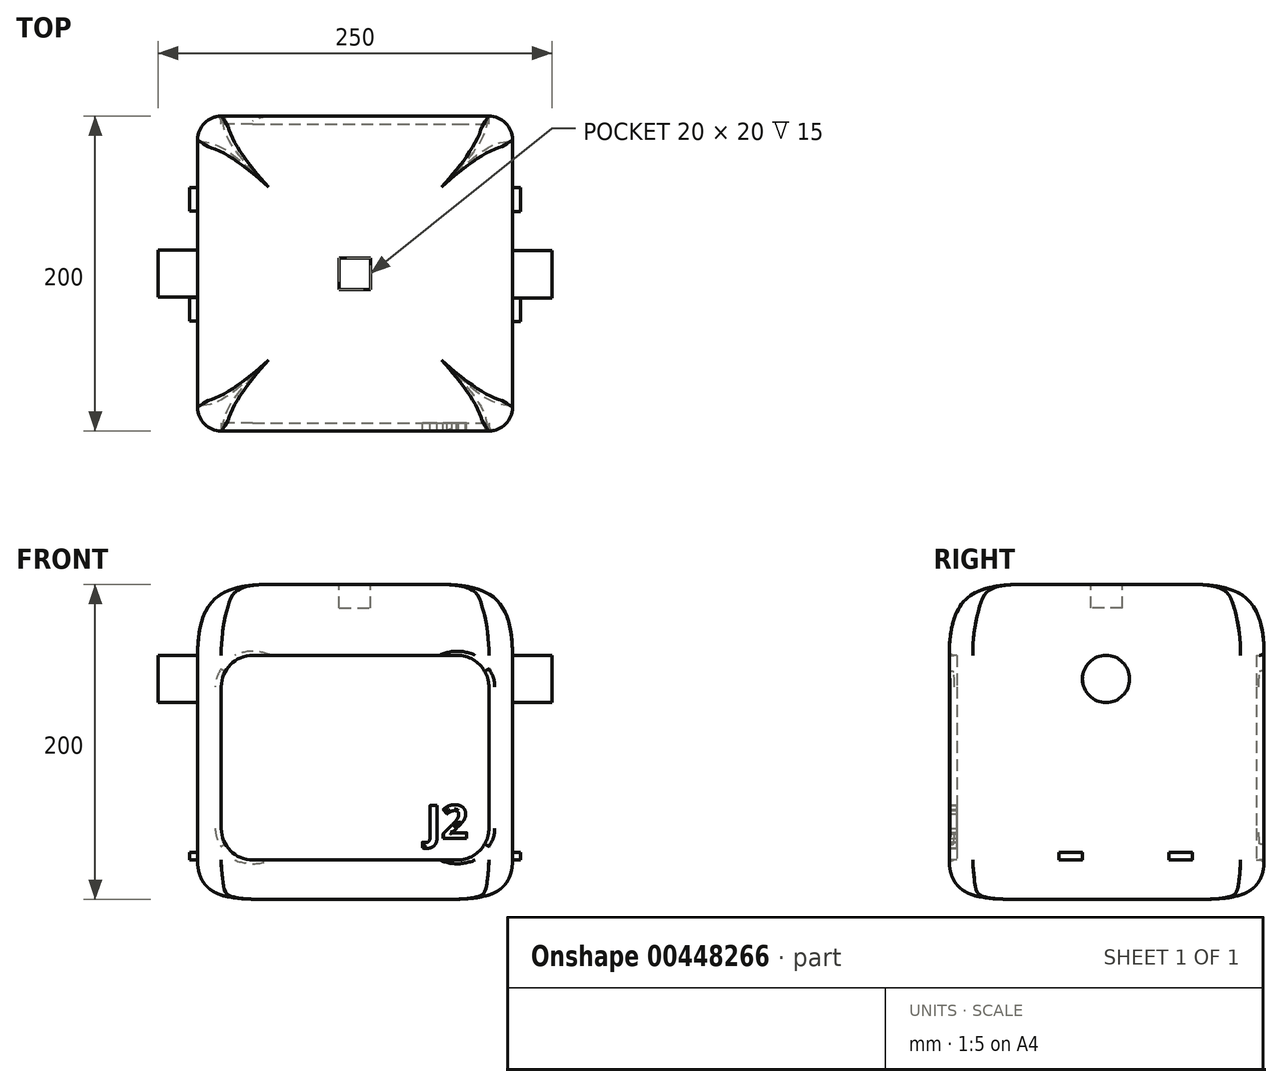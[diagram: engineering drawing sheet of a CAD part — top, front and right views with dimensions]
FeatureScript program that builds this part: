
annotation { "Feature Type Name" : "Feature", "Feature Type Description" : "" }
export const myFeature = defineFeature(function(context is Context, id is Id, definition is map)
    precondition{}
    {
        {
            var Q0;
            Q0=qCreatedBy(makeId("Front.planeOp"),FACE);
            var sketch = newSketch(context, id + "F0", { "sketchPlane" : qUnion([Q0])});
            skLineSegment(sketch, "E0.left", {"start": v(-100, 55) * mm, "end": v(-100, -75) * mm});
            skLineSegment(sketch, "E0.right", {"start": v(100, 100) * mm, "end": v(100, 90) * mm});
            skLineSegment(sketch, "E1.bottom", {"start": v(100, 100) * mm, "end": v(-100, 100) * mm, "construction": true});
            skLineSegment(sketch, "E1.top", {"start": v(100, -100) * mm, "end": v(-100, -100) * mm, "construction": true});
            skLineSegment(sketch, "E1.left", {"start": v(100, 100) * mm, "end": v(100, -100) * mm, "construction": true});
            skLineSegment(sketch, "E1.right", {"start": v(-100, 100) * mm, "end": v(-100, -100) * mm, "construction": true});
            skLineSegment(sketch, "E2", {"start": v(0, 100) * mm, "end": v(0, -100) * mm, "construction": true});
            skLineSegment(sketch, "E3", {"start": v(-100, 0) * mm, "end": v(100, 0) * mm, "construction": true});
            skLineSegment(sketch, "E4", {"start": v(100, -75) * mm, "end": v(-100, -75) * mm, "construction": true});
            skLineSegment(sketch, "E5", {"start": v(-100, 55) * mm, "end": v(100, 55) * mm, "construction": true});
            skLineSegment(sketch, "E6", {"start": v(-55, 100) * mm, "end": v(-55, -100) * mm, "construction": true});
            skLineSegment(sketch, "E7", {"start": v(55, 100) * mm, "end": v(55, -100) * mm, "construction": true});
            skLineSegment(sketch, "E8", {"start": v(-70, 100) * mm, "end": v(-70, -100) * mm, "construction": true});
            skLineSegment(sketch, "E9", {"start": v(70, 100) * mm, "end": v(70, -100) * mm, "construction": true});
            skLineSegment(sketch, "E10", {"start": v(-100, 70) * mm, "end": v(100, 70) * mm, "construction": true});
            skLineSegment(sketch, "E11", {"start": v(-100, -85) * mm, "end": v(100, -85) * mm, "construction": true});
            skLineSegment(sketch, "E12", {"start": v(-90, 100) * mm, "end": v(-90, -100) * mm, "construction": true});
            skLineSegment(sketch, "E13", {"start": v(90, 100) * mm, "end": v(90, -100) * mm, "construction": true});
            skLineSegment(sketch, "E14", {"start": v(-100, 90) * mm, "end": v(100, 90) * mm, "construction": true});
            skLineSegment(sketch, "E15", {"start": v(-100, -95) * mm, "end": v(100, -95) * mm, "construction": true});
            skFitSpline(sketch, "E16", {"points": [v(-55, 100) * mm, v(-90, 90) * mm, v(-100, 55) * mm], "startDerivative": vector(-90, 0) * mm, "endDerivative": vector(0, -90) * mm});
            skFitSpline(sketch, "E17", {"points": [v(55, 100) * mm, v(90, 90) * mm, v(100, 55) * mm], "startDerivative": vector(90, 0) * mm, "endDerivative": vector(0, -90) * mm});
            skFitSpline(sketch, "E18", {"points": [v(-55, -100) * mm, v(-90, -95) * mm, v(-100, -75) * mm], "startDerivative": vector(-80.79, 0) * mm, "endDerivative": vector(0, 67.72) * mm});
            skFitSpline(sketch, "E19", {"points": [v(55, -100) * mm, v(90, -95) * mm, v(100, -75) * mm], "startDerivative": vector(80.79, 0) * mm, "endDerivative": vector(0, 67.72) * mm});
            skLineSegment(sketch, "E20.trimOffspring", {"start": v(-55, 100) * mm, "end": v(55, 100) * mm});
            skLineSegment(sketch, "E21.trimOffspring", {"start": v(100, 55) * mm, "end": v(100, -75) * mm});
            skLineSegment(sketch, "E22.trimOffspring", {"start": v(-55, -100) * mm, "end": v(55, -100) * mm});
            skLineSegment(sketch, "E23", {"start": v(-100, -100) * mm, "end": v(100, -100) * mm, "construction": true});
            skLineSegment(sketch, "E24", {"start": v(-100, 100) * mm, "end": v(100, 100) * mm, "construction": true});
            skLineSegment(sketch, "E25", {"start": v(-100, -100) * mm, "end": v(-100, 100) * mm, "construction": true});
            skLineSegment(sketch, "E26", {"start": v(100, -100) * mm, "end": v(100, 100) * mm, "construction": true});
            skSolve(sketch);
        }
        {
            var Q0;
            Q0=makeQuery(id+"F0.imprint","IMPRINT",FACE,{"disambiguationData":[TD([[makeQuery(id+"F0.imprint","IMPRINT",EDGE,{"derivedFrom":sQuery(id+"F0.wireOp",EDGE,"E0.left")}),1.0]])]});
            extrude(context, id + "F1", {"entities" : qUnion([Q0]), "depth" : 200 * mm});
        }
        {
            var Q0;
            Q0=makeQuery(id+"F1.opExtrude","SWEPT_FACE",FACE,{"disambiguationData":[OSD([sQuery(id+"F0.wireOp",EDGE,"E21.trimOffspring")])]});
            var sketch = newSketch(context, id + "F2", { "sketchPlane" : qUnion([Q0])});
            skLineSegment(sketch, "E27", {"start": v(0, 100) * mm, "end": v(0, -100) * mm, "construction": true});
            skPoint(sketch, "E27.startSnap0", {"position": v(0, 0) * mm});
            skLineSegment(sketch, "E28", {"start": v(0, -100) * mm, "end": v(-200, -100) * mm, "construction": true});
            skLineSegment(sketch, "E29", {"start": v(-200, -100) * mm, "end": v(-200, 100) * mm, "construction": true});
            skLineSegment(sketch, "E30", {"start": v(-200, 100) * mm, "end": v(0, 100) * mm, "construction": true});
            skLineSegment(sketch, "E31.bottom", {"start": v(-175, 100) * mm, "end": v(25, 100) * mm, "construction": true});
            skLineSegment(sketch, "E31.top", {"start": v(-175, -100) * mm, "end": v(25, -100) * mm, "construction": true});
            skLineSegment(sketch, "E31.left", {"start": v(-175, 100) * mm, "end": v(-175, -100) * mm, "construction": true});
            skLineSegment(sketch, "E31.right", {"start": v(25, 100) * mm, "end": v(25, -100) * mm, "construction": true});
            skLineSegment(sketch, "E32", {"start": v(-100, 100) * mm, "end": v(-100, -100) * mm, "construction": true});
            skPoint(sketch, "E32.endSnap0", {"position": v(-100, -100) * mm});
            skLineSegment(sketch, "E33", {"start": v(-175, 0) * mm, "end": v(25, 0) * mm, "construction": true});
            skLineSegment(sketch, "E34", {"start": v(-155, 100) * mm, "end": v(-155, -100) * mm, "construction": true});
            skLineSegment(sketch, "E35", {"start": v(-170, 100) * mm, "end": v(-170, -100) * mm, "construction": true});
            skLineSegment(sketch, "E36", {"start": v(-45, 100) * mm, "end": v(-45, -100) * mm, "construction": true});
            skLineSegment(sketch, "E37", {"start": v(-30, 100) * mm, "end": v(-30, -100) * mm, "construction": true});
            skLineSegment(sketch, "E38", {"start": v(-200, 100) * mm, "end": v(-200, -100) * mm, "construction": true});
            skLineSegment(sketch, "E39", {"start": v(-190, 100) * mm, "end": v(-190, -100) * mm, "construction": true});
            skLineSegment(sketch, "E40", {"start": v(-10, 100) * mm, "end": v(-10, -100) * mm, "construction": true});
            skLineSegment(sketch, "E41", {"start": v(-175, 90) * mm, "end": v(25, 90) * mm, "construction": true});
            skLineSegment(sketch, "E42", {"start": v(-175, 70) * mm, "end": v(25, 70) * mm, "construction": true});
            skLineSegment(sketch, "E43", {"start": v(-175, 55) * mm, "end": v(25, 55) * mm, "construction": true});
            skLineSegment(sketch, "E44", {"start": v(-175, -85) * mm, "end": v(25, -85) * mm, "construction": true});
            skLineSegment(sketch, "E45", {"start": v(-175, -75) * mm, "end": v(25, -75) * mm, "construction": true});
            skLineSegment(sketch, "E46", {"start": v(-175, -95) * mm, "end": v(25, -95) * mm, "construction": true});
            skFitSpline(sketch, "E47", {"points": [v(-155, 100) * mm, v(-190, 90) * mm, v(-200, 55) * mm], "startDerivative": vector(-90, 0) * mm, "endDerivative": vector(0, -90) * mm});
            skFitSpline(sketch, "E48", {"points": [v(-45, 100) * mm, v(-10, 90) * mm, v(0, 55) * mm], "startDerivative": vector(90, 0) * mm, "endDerivative": vector(0, -90) * mm});
            skFitSpline(sketch, "E49", {"points": [v(-155, -100) * mm, v(-190, -95) * mm, v(-200, -75) * mm], "startDerivative": vector(-80.79, 0) * mm, "endDerivative": vector(0, 67.72) * mm});
            skFitSpline(sketch, "E50", {"points": [v(-45, -100) * mm, v(-10, -95) * mm, v(0, -75) * mm], "startDerivative": vector(80.79, 0) * mm, "endDerivative": vector(0, 67.72) * mm});
            skLineSegment(sketch, "E51", {"start": v(-155, 100) * mm, "end": v(-200, 100) * mm});
            skLineSegment(sketch, "E52", {"start": v(-200, 55) * mm, "end": v(-200, 100) * mm});
            skLineSegment(sketch, "E53", {"start": v(-200, -75) * mm, "end": v(-200, -100) * mm});
            skLineSegment(sketch, "E54", {"start": v(-200, -100) * mm, "end": v(-155, -100) * mm});
            skLineSegment(sketch, "E55", {"start": v(-45, -100) * mm, "end": v(0, -100) * mm});
            skLineSegment(sketch, "E56", {"start": v(0, -100) * mm, "end": v(0, -75) * mm});
            skLineSegment(sketch, "E57", {"start": v(0, 55) * mm, "end": v(0, 100) * mm});
            skLineSegment(sketch, "E58", {"start": v(-45, 100) * mm, "end": v(0, 100) * mm});
            skSolve(sketch);
        }
        {
            var Q0;
            Q0=makeQuery(id+"F2.imprint","IMPRINT",FACE,{"disambiguationData":[TD([[makeQuery(id+"F2.imprint","IMPRINT",EDGE,{"derivedFrom":sQuery(id+"F2.wireOp",EDGE,"E47")}),-1.0]])]});
            var Q1;
            Q1=makeQuery(id+"F2.imprint","IMPRINT",FACE,{"disambiguationData":[TD([[makeQuery(id+"F2.imprint","IMPRINT",EDGE,{"derivedFrom":sQuery(id+"F2.wireOp",EDGE,"E48")}),1.0]])]});
            var Q2;
            Q2=makeQuery(id+"F2.imprint","IMPRINT",FACE,{"disambiguationData":[TD([[makeQuery(id+"F2.imprint","IMPRINT",EDGE,{"derivedFrom":sQuery(id+"F2.wireOp",EDGE,"E50")}),-1.0]])]});
            var Q3;
            Q3=makeQuery(id+"F2.imprint","IMPRINT",FACE,{"disambiguationData":[TD([[makeQuery(id+"F2.imprint","IMPRINT",EDGE,{"derivedFrom":sQuery(id+"F2.wireOp",EDGE,"E49")}),1.0]])]});
            extrude(context, id + "F3", {"entities" : qUnion([Q0, Q1, Q2, Q3]), "operationType" : NewBodyOperationType.REMOVE, "oppositeDirection" : true, "depth" : 200 * mm});
        }
        {
            var Q0;
            Q0=makeQuery(id+"F1.opExtrude","CAP_EDGE",EDGE,{"disambiguationData":[OSD([sQuery(id+"F0.wireOp",EDGE,"E0.left")])],"isStart":false});
            var Q1;
            Q1=makeQuery(id+"F1.opExtrude","CAP_EDGE",EDGE,{"disambiguationData":[OSD([sQuery(id+"F0.wireOp",EDGE,"E21.trimOffspring")])],"isStart":false});
            fillet(context, id + "F4", {"entities" : qUnion([Q0, Q1]), "radius" : 15 * mm, "tangentPropagation" : true, "allowEdgeOverflow" : false});
        }
        {
            var Q0;
            Q0=makeQuery(id+"F1.opExtrude","SWEPT_FACE",FACE,{"disambiguationData":[OSD([sQuery(id+"F0.wireOp",EDGE,"E0.left")])]});
            var Q1;
            Q1=makeQuery(id+"F3.boolean.opBoolean","INTERSECT",EDGE,{"derivedFrom":[makeQuery(id+"F1.opExtrude","SWEPT_FACE",FACE,{"disambiguationData":[OSD([sQuery(id+"F0.wireOp",EDGE,"E16")])]}),makeQuery(id+"F3.opExtrude","SWEPT_FACE",FACE,{"disambiguationData":[OSD([sQuery(id+"F2.wireOp",EDGE,"E48")])]})]});
            var Q2;
            Q2=makeQuery(id+"F3.boolean.opBoolean","INTERSECT",EDGE,{"derivedFrom":[makeQuery(id+"F1.opExtrude","SWEPT_FACE",FACE,{"disambiguationData":[OSD([sQuery(id+"F0.wireOp",EDGE,"E18")])]}),makeQuery(id+"F3.opExtrude","SWEPT_FACE",FACE,{"disambiguationData":[OSD([sQuery(id+"F2.wireOp",EDGE,"E50")])]})]});
            var Q3;
            Q3=makeQuery(id+"F1.opExtrude","SWEPT_FACE",FACE,{"disambiguationData":[OSD([sQuery(id+"F0.wireOp",EDGE,"E21.trimOffspring")])]});
            var Q4;
            Q4=makeQuery(id+"F3.boolean.opBoolean","INTERSECT",EDGE,{"derivedFrom":[makeQuery(id+"F1.opExtrude","SWEPT_FACE",FACE,{"disambiguationData":[OSD([sQuery(id+"F0.wireOp",EDGE,"E17")])]}),makeQuery(id+"F3.opExtrude","SWEPT_FACE",FACE,{"disambiguationData":[OSD([sQuery(id+"F2.wireOp",EDGE,"E48")])]})]});
            var Q5;
            Q5=makeQuery(id+"F3.boolean.opBoolean","INTERSECT",EDGE,{"derivedFrom":[makeQuery(id+"F1.opExtrude","SWEPT_FACE",FACE,{"disambiguationData":[OSD([sQuery(id+"F0.wireOp",EDGE,"E19")])]}),makeQuery(id+"F3.opExtrude","SWEPT_FACE",FACE,{"disambiguationData":[OSD([sQuery(id+"F2.wireOp",EDGE,"E50")])]})]});
            fillet(context, id + "F5", {"entities" : qUnion([Q0, Q1, Q2, Q3, Q4, Q5]), "radius" : 15 * mm, "tangentPropagation" : true, "allowEdgeOverflow" : false});
        }
        {
            var Q0;
            Q0=makeQuery(id+"F1.opExtrude","CAP_FACE",FACE,{"disambiguationData":[OSD([sQuery(id+"F0.wireOp",EDGE,"E0.left"),sQuery(id+"F0.wireOp",EDGE,"E16"),sQuery(id+"F0.wireOp",EDGE,"E17"),sQuery(id+"F0.wireOp",EDGE,"E18"),sQuery(id+"F0.wireOp",EDGE,"E19"),sQuery(id+"F0.wireOp",EDGE,"E20.trimOffspring"),sQuery(id+"F0.wireOp",EDGE,"E21.trimOffspring"),sQuery(id+"F0.wireOp",EDGE,"E22.trimOffspring")])],"isStart":false});
            var sketch = newSketch(context, id + "F6", { "sketchPlane" : qUnion([Q0])});
            skLineSegment(sketch, "E59", {"start": v(-65, 55) * mm, "end": v(65, 55) * mm, "construction": true});
            skLineSegment(sketch, "E60", {"start": v(85, 35) * mm, "end": v(85, -55) * mm, "construction": true});
            skLineSegment(sketch, "E61", {"start": v(65, -75) * mm, "end": v(-65, -75) * mm, "construction": true});
            skLineSegment(sketch, "E62", {"start": v(-85, -55) * mm, "end": v(-85, 35) * mm, "construction": true});
            skLineSegment(sketch, "E63.bottom", {"start": v(-65, 55) * mm, "end": v(65, 55) * mm});
            skLineSegment(sketch, "E63.top", {"start": v(-65, -75) * mm, "end": v(65, -75) * mm});
            skLineSegment(sketch, "E63.left", {"start": v(-85, 35) * mm, "end": v(-85, -55) * mm});
            skLineSegment(sketch, "E63.right", {"start": v(85, 35) * mm, "end": v(85, -55) * mm});
            skPoint(sketch, "E64.visualSharp", {"position": v(-85, 55) * mm});
            skArc(sketch, "E64.filletArc", {"start": v(-65, 55) * mm, "mid": v(-79.14, 49.14) * mm, "end": v(-85, 35) * mm});
            skPoint(sketch, "E65.visualSharp", {"position": v(85, 55) * mm});
            skArc(sketch, "E65.filletArc", {"start": v(85, 35) * mm, "mid": v(79.14, 49.14) * mm, "end": v(65, 55) * mm});
            skPoint(sketch, "E66.visualSharp", {"position": v(85, -75) * mm});
            skArc(sketch, "E66.filletArc", {"start": v(65, -75) * mm, "mid": v(79.14, -69.14) * mm, "end": v(85, -55) * mm});
            skPoint(sketch, "E67.visualSharp", {"position": v(-85, -75) * mm});
            skArc(sketch, "E67.filletArc", {"start": v(-85, -55) * mm, "mid": v(-79.14, -69.14) * mm, "end": v(-65, -75) * mm});
            skSolve(sketch);
        }
        {
            var Q0;
            {var subQ0=sQuery(id+"F6.wireOp",EDGE,"E63.bottom");Q0=makeQuery(id+"F6.imprint","IMPRINT",FACE,{"disambiguationData":[TD([[makeQuery(id+"F6.imprint","IMPRINT",EDGE,{"derivedFrom":subQ0}),-1.0]])]});}
            var Q1;
            {var subQ11=sQuery(id+"F6.wireOp",EDGE,"E63.left");Q1=makeQuery(id+"F6.imprint","IMPRINT",FACE,{"disambiguationData":[TD([[makeQuery(id+"F6.imprint","IMPRINT",EDGE,{"derivedFrom":subQ11}),1.0]])]});}
            var Q2;
            {var subQ0=sQuery(id+"F6.wireOp",EDGE,"E63.top");Q2=makeQuery(id+"F6.imprint","IMPRINT",FACE,{"disambiguationData":[TD([[makeQuery(id+"F6.imprint","IMPRINT",EDGE,{"derivedFrom":subQ0}),1.0]])]});}
            extrude(context, id + "F7", {"entities" : qUnion([Q0, Q1, Q2]), "operationType" : NewBodyOperationType.REMOVE, "oppositeDirection" : true, "depth" : 5 * mm});
        }
        {
            var Q0;
            Q0=makeQuery(id+"F1.opExtrude","CAP_FACE",FACE,{"disambiguationData":[OSD([sQuery(id+"F0.wireOp",EDGE,"E0.left"),sQuery(id+"F0.wireOp",EDGE,"E16"),sQuery(id+"F0.wireOp",EDGE,"E17"),sQuery(id+"F0.wireOp",EDGE,"E18"),sQuery(id+"F0.wireOp",EDGE,"E19"),sQuery(id+"F0.wireOp",EDGE,"E20.trimOffspring"),sQuery(id+"F0.wireOp",EDGE,"E21.trimOffspring"),sQuery(id+"F0.wireOp",EDGE,"E22.trimOffspring")])],"isStart":true});
            var sketch = newSketch(context, id + "F8", { "sketchPlane" : qUnion([Q0])});
            skLineSegment(sketch, "E68", {"start": v(-65, 55) * mm, "end": v(65, 55) * mm, "construction": true});
            skLineSegment(sketch, "E69", {"start": v(85, 35) * mm, "end": v(85, -55) * mm, "construction": true});
            skLineSegment(sketch, "E70", {"start": v(65, -75) * mm, "end": v(-65, -75) * mm, "construction": true});
            skLineSegment(sketch, "E71", {"start": v(-85, -55) * mm, "end": v(-85, 35) * mm, "construction": true});
            skLineSegment(sketch, "E72.bottom", {"start": v(-65, 55) * mm, "end": v(65, 55) * mm});
            skLineSegment(sketch, "E72.top", {"start": v(-65, -75) * mm, "end": v(65, -75) * mm});
            skLineSegment(sketch, "E72.left", {"start": v(-85, 35) * mm, "end": v(-85, -55) * mm});
            skLineSegment(sketch, "E72.right", {"start": v(85, 35) * mm, "end": v(85, -55) * mm});
            skPoint(sketch, "E73.visualSharp", {"position": v(-85, 55) * mm});
            skArc(sketch, "E73.filletArc", {"start": v(-65, 55) * mm, "mid": v(-79.14, 49.14) * mm, "end": v(-85, 35) * mm});
            skPoint(sketch, "E74.visualSharp", {"position": v(85, 55) * mm});
            skArc(sketch, "E74.filletArc", {"start": v(85, 35) * mm, "mid": v(79.14, 49.14) * mm, "end": v(65, 55) * mm});
            skPoint(sketch, "E75.visualSharp", {"position": v(85, -75) * mm});
            skArc(sketch, "E75.filletArc", {"start": v(65, -75) * mm, "mid": v(79.14, -69.14) * mm, "end": v(85, -55) * mm});
            skPoint(sketch, "E76.visualSharp", {"position": v(-85, -75) * mm});
            skArc(sketch, "E76.filletArc", {"start": v(-85, -55) * mm, "mid": v(-79.14, -69.14) * mm, "end": v(-65, -75) * mm});
            skLineSegment(sketch, "E77", {"start": v(-85, 96.83) * mm, "end": v(-85, -55.3) * mm, "construction": true});
            skLineSegment(sketch, "E78", {"start": v(85, 80.25) * mm, "end": v(85, -73.47) * mm, "construction": true});
            skSolve(sketch);
        }
        {
            var Q0;
            {var subQ11=sQuery(id+"F8.wireOp",EDGE,"E72.left");Q0=makeQuery(id+"F8.imprint","IMPRINT",FACE,{"disambiguationData":[TD([[makeQuery(id+"F8.imprint","IMPRINT",EDGE,{"derivedFrom":subQ11}),1.0]])]});}
            var Q1;
            {var subQ0=sQuery(id+"F8.wireOp",EDGE,"E72.bottom");Q1=makeQuery(id+"F8.imprint","IMPRINT",FACE,{"disambiguationData":[TD([[makeQuery(id+"F8.imprint","IMPRINT",EDGE,{"derivedFrom":subQ0}),-1.0]])]});}
            var Q2;
            {var subQ0=sQuery(id+"F8.wireOp",EDGE,"E72.top");Q2=makeQuery(id+"F8.imprint","IMPRINT",FACE,{"disambiguationData":[TD([[makeQuery(id+"F8.imprint","IMPRINT",EDGE,{"derivedFrom":subQ0}),1.0]])]});}
            extrude(context, id + "F9", {"entities" : qUnion([Q0, Q1, Q2]), "operationType" : NewBodyOperationType.REMOVE, "oppositeDirection" : true, "depth" : 5 * mm});
        }
        {
            var Q0;
            {var subQ0=sQuery(id+"F0.wireOp",EDGE,"E21.trimOffspring");Q0=makeQuery(id+"F7.boolean.opBoolean","MERGE",EDGE,{"derivedFrom":[makeQuery(id+"F4.opFillet","BLEND_EDGE",EDGE,{"blendedFrom":[makeQuery(id+"F1.opExtrude","CAP_EDGE",EDGE,{"disambiguationData":[OSD([subQ0])],"isStart":false}),makeQuery(id+"F1.opExtrude","CAP_FACE",FACE,{"disambiguationData":[OSD([sQuery(id+"F0.wireOp",EDGE,"E0.left"),sQuery(id+"F0.wireOp",EDGE,"E16"),sQuery(id+"F0.wireOp",EDGE,"E17"),sQuery(id+"F0.wireOp",EDGE,"E18"),sQuery(id+"F0.wireOp",EDGE,"E19"),sQuery(id+"F0.wireOp",EDGE,"E20.trimOffspring"),subQ0,sQuery(id+"F0.wireOp",EDGE,"E22.trimOffspring")])],"isStart":false})],"blendedInto":[makeQuery(id+"F1.opExtrude","CAP_FACE",FACE,{"disambiguationData":[OSD([sQuery(id+"F0.wireOp",EDGE,"E0.left"),sQuery(id+"F0.wireOp",EDGE,"E16"),sQuery(id+"F0.wireOp",EDGE,"E17"),sQuery(id+"F0.wireOp",EDGE,"E18"),sQuery(id+"F0.wireOp",EDGE,"E19"),sQuery(id+"F0.wireOp",EDGE,"E20.trimOffspring"),subQ0,sQuery(id+"F0.wireOp",EDGE,"E22.trimOffspring")])],"isStart":false})]}),makeQuery(id+"F7.opExtrude","CAP_EDGE",EDGE,{"disambiguationData":[OSD([sQuery(id+"F6.wireOp",EDGE,"E63.right")])],"isStart":true})]});}
            var Q1;
            {var subQ0=sQuery(id+"F0.wireOp",EDGE,"E0.left");Q1=makeQuery(id+"F9.boolean.opBoolean","MERGE",EDGE,{"derivedFrom":[makeQuery(id+"F5.opFillet","BLEND_EDGE",EDGE,{"blendedFrom":[makeQuery(id+"F1.opExtrude","CAP_EDGE",EDGE,{"disambiguationData":[OSD([subQ0])],"isStart":true}),makeQuery(id+"F1.opExtrude","CAP_FACE",FACE,{"disambiguationData":[OSD([subQ0,sQuery(id+"F0.wireOp",EDGE,"E16"),sQuery(id+"F0.wireOp",EDGE,"E17"),sQuery(id+"F0.wireOp",EDGE,"E18"),sQuery(id+"F0.wireOp",EDGE,"E19"),sQuery(id+"F0.wireOp",EDGE,"E20.trimOffspring"),sQuery(id+"F0.wireOp",EDGE,"E21.trimOffspring"),sQuery(id+"F0.wireOp",EDGE,"E22.trimOffspring")])],"isStart":true})],"blendedInto":[makeQuery(id+"F1.opExtrude","CAP_FACE",FACE,{"disambiguationData":[OSD([subQ0,sQuery(id+"F0.wireOp",EDGE,"E16"),sQuery(id+"F0.wireOp",EDGE,"E17"),sQuery(id+"F0.wireOp",EDGE,"E18"),sQuery(id+"F0.wireOp",EDGE,"E19"),sQuery(id+"F0.wireOp",EDGE,"E20.trimOffspring"),sQuery(id+"F0.wireOp",EDGE,"E21.trimOffspring"),sQuery(id+"F0.wireOp",EDGE,"E22.trimOffspring")])],"isStart":true})]}),makeQuery(id+"F9.opExtrude","CAP_EDGE",EDGE,{"disambiguationData":[OSD([sQuery(id+"F8.wireOp",EDGE,"E72.right")])],"isStart":true})]});}
            fillet(context, id + "F10", {"entities" : qUnion([Q0, Q1]), "radius" : 3 * mm, "tangentPropagation" : true, "allowEdgeOverflow" : false});
        }
        {
            var Q0;
            Q0=makeQuery(id+"F7.boolean.opBoolean","COPY",FACE,{"derivedFrom":makeQuery(id+"F7.opExtrude","CAP_FACE",FACE,{"disambiguationData":[OSD([sQuery(id+"F6.wireOp",EDGE,"E63.bottom"),sQuery(id+"F6.wireOp",EDGE,"E63.top"),sQuery(id+"F6.wireOp",EDGE,"E63.left"),sQuery(id+"F6.wireOp",EDGE,"E63.right"),sQuery(id+"F6.wireOp",EDGE,"E64.filletArc"),sQuery(id+"F6.wireOp",EDGE,"E65.filletArc"),sQuery(id+"F6.wireOp",EDGE,"E66.filletArc"),sQuery(id+"F6.wireOp",EDGE,"E67.filletArc")])],"isStart":false})});
            var sketch = newSketch(context, id + "F11", { "sketchPlane" : qUnion([Q0])});
            skText(sketch, "E79", { "text": "J2", "fontName": "OpenSans-Bold.ttf"});
            const initialGuessF11  = {"E79": [0.045, -0.0614, 1, 0, 0.0214]};
            skSetInitialGuess(sketch, initialGuessF11);
            skSolve(sketch);
        }
        {
            var Q0;
            Q0 = qSketchRegion(id + "F11", true);
            extrude(context, id + "F12", {"entities" : qUnion([Q0]), "operationType" : NewBodyOperationType.ADD, "depth" : 5 * mm});
        }
        {
            var Q0;
            Q0=makeQuery(id+"F12.opExtrude","CAP_EDGE",EDGE,{"disambiguationData":[OSD([sQuery(id+"F11.wireOp",EDGE,"E79.sketch_text.stroke-5")])],"isStart":false});
            var Q1;
            Q1=makeQuery(id+"F12.opExtrude","CAP_EDGE",EDGE,{"disambiguationData":[OSD([sQuery(id+"F11.wireOp",EDGE,"E79.sketch_text.stroke-6")])],"isStart":false});
            var Q2;
            Q2=makeQuery(id+"F12.opExtrude","CAP_EDGE",EDGE,{"disambiguationData":[OSD([sQuery(id+"F11.wireOp",EDGE,"E79.sketch_text.stroke-7")])],"isStart":false});
            var Q3;
            Q3=makeQuery(id+"F12.opExtrude","CAP_EDGE",EDGE,{"disambiguationData":[OSD([sQuery(id+"F11.wireOp",EDGE,"E79.sketch_text.stroke-8")])],"isStart":false});
            var Q4;
            Q4=makeQuery(id+"F12.opExtrude","CAP_EDGE",EDGE,{"disambiguationData":[OSD([sQuery(id+"F11.wireOp",EDGE,"E79.sketch_text.stroke-1")])],"isStart":false});
            var Q5;
            Q5=makeQuery(id+"F12.opExtrude","CAP_FACE",FACE,{"disambiguationData":[OSD([sQuery(id+"F11.wireOp",EDGE,"E79.sketch_text.stroke-10"),sQuery(id+"F11.wireOp",EDGE,"E79.sketch_text.stroke-11"),sQuery(id+"F11.wireOp",EDGE,"E79.sketch_text.stroke-12"),sQuery(id+"F11.wireOp",EDGE,"E79.sketch_text.stroke-13"),sQuery(id+"F11.wireOp",EDGE,"E79.sketch_text.stroke-14"),sQuery(id+"F11.wireOp",EDGE,"E79.sketch_text.stroke-15"),sQuery(id+"F11.wireOp",EDGE,"E79.sketch_text.stroke-16"),sQuery(id+"F11.wireOp",EDGE,"E79.sketch_text.stroke-17"),sQuery(id+"F11.wireOp",EDGE,"E79.sketch_text.stroke-18"),sQuery(id+"F11.wireOp",EDGE,"E79.sketch_text.stroke-19"),sQuery(id+"F11.wireOp",EDGE,"E79.sketch_text.stroke-20"),sQuery(id+"F11.wireOp",EDGE,"E79.sketch_text.stroke-21"),sQuery(id+"F11.wireOp",EDGE,"E79.sketch_text.stroke-22"),sQuery(id+"F11.wireOp",EDGE,"E79.sketch_text.stroke-23"),sQuery(id+"F11.wireOp",EDGE,"E79.sketch_text.stroke-24"),sQuery(id+"F11.wireOp",EDGE,"E79.sketch_text.stroke-25"),sQuery(id+"F11.wireOp",EDGE,"E79.sketch_text.stroke-26"),sQuery(id+"F11.wireOp",EDGE,"E79.sketch_text.stroke-27"),sQuery(id+"F11.wireOp",EDGE,"E79.sketch_text.stroke-28"),sQuery(id+"F11.wireOp",EDGE,"E79.sketch_text.stroke-29"),sQuery(id+"F11.wireOp",EDGE,"E79.sketch_text.stroke-30"),sQuery(id+"F11.wireOp",EDGE,"E79.sketch_text.stroke-31"),sQuery(id+"F11.wireOp",EDGE,"E79.sketch_text.stroke-32"),sQuery(id+"F11.wireOp",EDGE,"E79.sketch_text.stroke-33")])],"isStart":false});
            fillet(context, id + "F13", {"entities" : qUnion([Q0, Q1, Q2, Q3, Q4, Q5]), "radius" : 1 * mm, "tangentPropagation" : true, "allowEdgeOverflow" : false});
        }
        {
            var Q0;
            Q0=makeQuery(id+"F1.opExtrude","SWEPT_FACE",FACE,{"disambiguationData":[OSD([sQuery(id+"F0.wireOp",EDGE,"E21.trimOffspring")])]});
            var sketch = newSketch(context, id + "F14", { "sketchPlane" : qUnion([Q0])});
            skCircle(sketch, "E80", {"center": v(-60.48, -50) * mm, "radius": 30 * mm, "construction": true});
            skCircle(sketch, "E81", {"center": v(-5.48, -120) * mm, "radius": 30 * mm, "construction": true});
            skCircle(sketch, "E82", {"center": v(-165.48, -120) * mm, "radius": 30 * mm, "construction": true});
            skLineSegment(sketch, "E83.left", {"start": v(-130.48, -70) * mm, "end": v(-130.48, -75) * mm});
            skLineSegment(sketch, "E83.right", {"start": v(-115.48, -70) * mm, "end": v(-115.48, -75) * mm});
            skLineSegment(sketch, "E84.left", {"start": v(-60.48, -70) * mm, "end": v(-60.48, -75) * mm});
            skLineSegment(sketch, "E84.right", {"start": v(-45.48, -70) * mm, "end": v(-45.48, -75) * mm});
            skLineSegment(sketch, "E85", {"start": v(-147.43, -70) * mm, "end": v(31.34, -70) * mm, "construction": true});
            skLineSegment(sketch, "E86", {"start": v(-146.82, -75) * mm, "end": v(31.75, -75) * mm, "construction": true});
            skLineSegment(sketch, "E87", {"start": v(-130.48, -70) * mm, "end": v(-115.48, -70) * mm});
            skLineSegment(sketch, "E88", {"start": v(-115.48, -75) * mm, "end": v(-130.48, -75) * mm});
            skLineSegment(sketch, "E89", {"start": v(-60.48, -70) * mm, "end": v(-45.48, -70) * mm});
            skLineSegment(sketch, "E90", {"start": v(-45.48, -75) * mm, "end": v(-60.48, -75) * mm});
            skLineSegment(sketch, "E91", {"start": v(0, 0) * mm, "end": v(-231.4, 0) * mm, "construction": true});
            skSolve(sketch);
        }
        {
            var Q0;
            Q0=makeQuery(id+"F14.imprint","IMPRINT",FACE,{"disambiguationData":[TD([[makeQuery(id+"F14.imprint","IMPRINT",EDGE,{"derivedFrom":sQuery(id+"F14.wireOp",EDGE,"E83.left")}),1.0]])]});
            var Q1;
            Q1=makeQuery(id+"F14.imprint","IMPRINT",FACE,{"disambiguationData":[TD([[makeQuery(id+"F14.imprint","IMPRINT",EDGE,{"derivedFrom":sQuery(id+"F14.wireOp",EDGE,"E84.left")}),1.0]])]});
            extrude(context, id + "F15", {"entities" : qUnion([Q0, Q1]), "operationType" : NewBodyOperationType.ADD, "depth" : 5 * mm});
        }
        {
            var Q0;
            Q0=makeQuery(id+"F1.opExtrude","SWEPT_FACE",FACE,{"disambiguationData":[OSD([sQuery(id+"F0.wireOp",EDGE,"E0.left")])]});
            var sketch = newSketch(context, id + "F16", { "sketchPlane" : qUnion([Q0])});
            skLineSegment(sketch, "E92.left", {"start": v(45.26, -70) * mm, "end": v(45.26, -75) * mm});
            skLineSegment(sketch, "E92.right", {"start": v(60.26, -70) * mm, "end": v(60.26, -75) * mm});
            skLineSegment(sketch, "E93.left", {"start": v(115.26, -70) * mm, "end": v(115.26, -75) * mm});
            skLineSegment(sketch, "E93.right", {"start": v(130.26, -70) * mm, "end": v(130.26, -75) * mm});
            skLineSegment(sketch, "E94", {"start": v(-46.63, -70) * mm, "end": v(132.15, -70) * mm, "construction": true});
            skLineSegment(sketch, "E95", {"start": v(-46, -75) * mm, "end": v(132.56, -75) * mm, "construction": true});
            skLineSegment(sketch, "E96", {"start": v(45.26, -70) * mm, "end": v(60.26, -70) * mm});
            skLineSegment(sketch, "E97", {"start": v(60.26, -75) * mm, "end": v(45.26, -75) * mm});
            skLineSegment(sketch, "E98", {"start": v(115.26, -70) * mm, "end": v(130.26, -70) * mm});
            skLineSegment(sketch, "E99", {"start": v(130.26, -75) * mm, "end": v(115.26, -75) * mm});
            skSolve(sketch);
        }
        {
            var Q0;
            Q0=makeQuery(id+"F16.imprint","IMPRINT",FACE,{"disambiguationData":[TD([[makeQuery(id+"F16.imprint","IMPRINT",EDGE,{"derivedFrom":sQuery(id+"F16.wireOp",EDGE,"E93.left")}),1.0]])]});
            var Q1;
            Q1=makeQuery(id+"F16.imprint","IMPRINT",FACE,{"disambiguationData":[TD([[makeQuery(id+"F16.imprint","IMPRINT",EDGE,{"derivedFrom":sQuery(id+"F16.wireOp",EDGE,"E92.left")}),1.0]])]});
            extrude(context, id + "F17", {"entities" : qUnion([Q0, Q1]), "operationType" : NewBodyOperationType.ADD, "depth" : 5 * mm});
        }
        {
            var Q0;
            Q0=makeQuery(id+"F1.opExtrude","SWEPT_FACE",FACE,{"disambiguationData":[OSD([sQuery(id+"F0.wireOp",EDGE,"E20.trimOffspring")])]});
            var sketch = newSketch(context, id + "F18", { "sketchPlane" : qUnion([Q0])});
            skLineSegment(sketch, "E100.bottom", {"start": v(-10, -90) * mm, "end": v(10, -90) * mm});
            skLineSegment(sketch, "E100.top", {"start": v(-10, -110) * mm, "end": v(10, -110) * mm});
            skLineSegment(sketch, "E100.left", {"start": v(-10, -90) * mm, "end": v(-10, -110) * mm});
            skLineSegment(sketch, "E100.right", {"start": v(10, -90) * mm, "end": v(10, -110) * mm});
            skSolve(sketch);
        }
        {
            var Q0;
            Q0=makeQuery(id+"F18.imprint","IMPRINT",FACE,{"disambiguationData":[TD([[makeQuery(id+"F18.imprint","IMPRINT",EDGE,{"derivedFrom":sQuery(id+"F18.wireOp",EDGE,"E100.bottom")}),-1.0]])]});
            extrude(context, id + "F19", {"entities" : qUnion([Q0]), "operationType" : NewBodyOperationType.REMOVE, "oppositeDirection" : true, "depth" : 15 * mm});
        }
        {
            var Q0;
            Q0=makeQuery(id+"F1.opExtrude","SWEPT_FACE",FACE,{"disambiguationData":[OSD([sQuery(id+"F0.wireOp",EDGE,"E0.left")])]});
            var sketch = newSketch(context, id + "F20", { "sketchPlane" : qUnion([Q0])});
            skCircle(sketch, "E101", {"center": v(100, 40) * mm, "radius": 15 * mm});
            skSolve(sketch);
        }
        {
            var Q0;
            Q0=makeQuery(id+"F20.imprint","IMPRINT",FACE,{"disambiguationData":[TD([[makeQuery(id+"F20.imprint","IMPRINT",EDGE,{"derivedFrom":sQuery(id+"F20.wireOp",EDGE,"sE0PQOoL-99et-AA2k-1MY5-X4kO1e4xxGpb")}),1.0]])]});
            var Q1;
            Q1=makeQuery(id+"F20.imprint","IMPRINT",FACE,{"disambiguationData":[TD([[makeQuery(id+"F20.imprint","IMPRINT",EDGE,{"derivedFrom":sQuery(id+"F20.wireOp",EDGE,"E101")}),1.0]])]});
            extrude(context, id + "F21", {"entities" : qUnion([Q0, Q1]), "operationType" : NewBodyOperationType.ADD, "depth" : 25 * mm});
        }
        {
            var Q0;
            Q0=makeQuery(id+"F1.opExtrude","SWEPT_FACE",FACE,{"disambiguationData":[OSD([sQuery(id+"F0.wireOp",EDGE,"E21.trimOffspring")])]});
            var sketch = newSketch(context, id + "F22", { "sketchPlane" : qUnion([Q0])});
            skCircle(sketch, "E102", {"center": v(-100.48, 40) * mm, "radius": 15 * mm});
            skSolve(sketch);
        }
        {
            var Q0;
            Q0=makeQuery(id+"F22.imprint","IMPRINT",FACE,{"disambiguationData":[TD([[makeQuery(id+"F22.imprint","IMPRINT",EDGE,{"derivedFrom":sQuery(id+"F22.wireOp",EDGE,"wO7GOrR5-NJhU-MgQ4-CWMg-ZodSOYX7ipfx")}),1.0]])]});
            var Q1;
            Q1=makeQuery(id+"F22.imprint","IMPRINT",FACE,{"disambiguationData":[TD([[makeQuery(id+"F22.imprint","IMPRINT",EDGE,{"derivedFrom":sQuery(id+"F22.wireOp",EDGE,"E102")}),1.0]])]});
            extrude(context, id + "F23", {"entities" : qUnion([Q0, Q1]), "operationType" : NewBodyOperationType.ADD, "depth" : 25 * mm});
        }
    });
